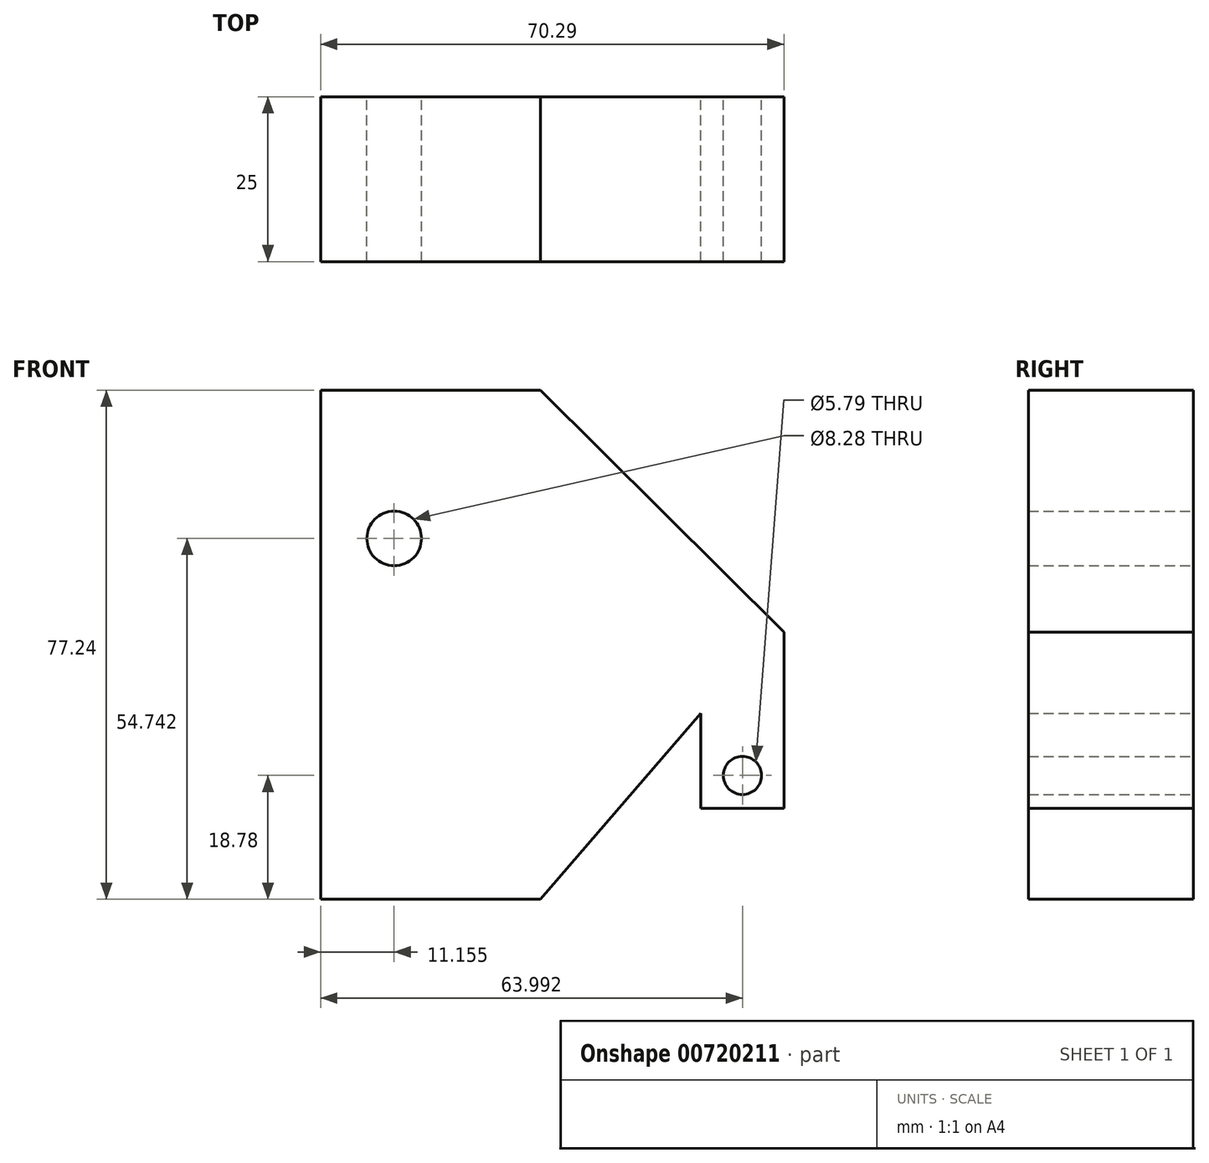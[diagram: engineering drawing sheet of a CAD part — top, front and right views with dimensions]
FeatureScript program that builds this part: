
annotation { "Feature Type Name" : "Feature", "Feature Type Description" : "" }
export const myFeature = defineFeature(function(context is Context, id is Id, definition is map)
    precondition{}
    {
        {
            var Q0;
            Q0=qCreatedBy(makeId("Front.planeOp"),FACE);
            var sketch = newSketch(context, id + "F0", { "sketchPlane" : qUnion([Q0])});
            skLineSegment(sketch, "E0", {"start": v(0, 0) * mm, "end": v(0, 26.73) * mm});
            skLineSegment(sketch, "E1", {"start": v(0, 26.73) * mm, "end": v(-36.93, 63.46) * mm});
            skLineSegment(sketch, "E2", {"start": v(-36.93, 63.46) * mm, "end": v(-70.29, 63.46) * mm});
            skLineSegment(sketch, "E3", {"start": v(-70.29, 63.46) * mm, "end": v(-70.29, -13.78) * mm});
            skLineSegment(sketch, "E4", {"start": v(-70.29, -13.78) * mm, "end": v(-36.93, -13.78) * mm});
            skLineSegment(sketch, "E5", {"start": v(-36.93, -13.78) * mm, "end": v(-12.6, 14.42) * mm});
            skLineSegment(sketch, "E6", {"start": v(-12.6, 14.42) * mm, "end": v(-12.6, 0) * mm});
            skLineSegment(sketch, "E7", {"start": v(-12.6, 0) * mm, "end": v(0, 0) * mm});
            skCircle(sketch, "E8", {"center": v(-6.3, 5) * mm, "radius": 2.9 * mm});
            skPoint(sketch, "E8.centerSnap0", {"position": v(-6.3, 0) * mm});
            skCircle(sketch, "E9", {"center": v(-59.13, 40.96) * mm, "radius": 4.14 * mm});
            skSolve(sketch);
        }
        {
            var Q0;
            Q0 = qSketchRegion(id + "F0", true);
            extrude(context, id + "F1", {"entities" : qUnion([Q0]), "depth" : 25 * mm, "offsetDistance" : 25 * mm});
        }
    });
